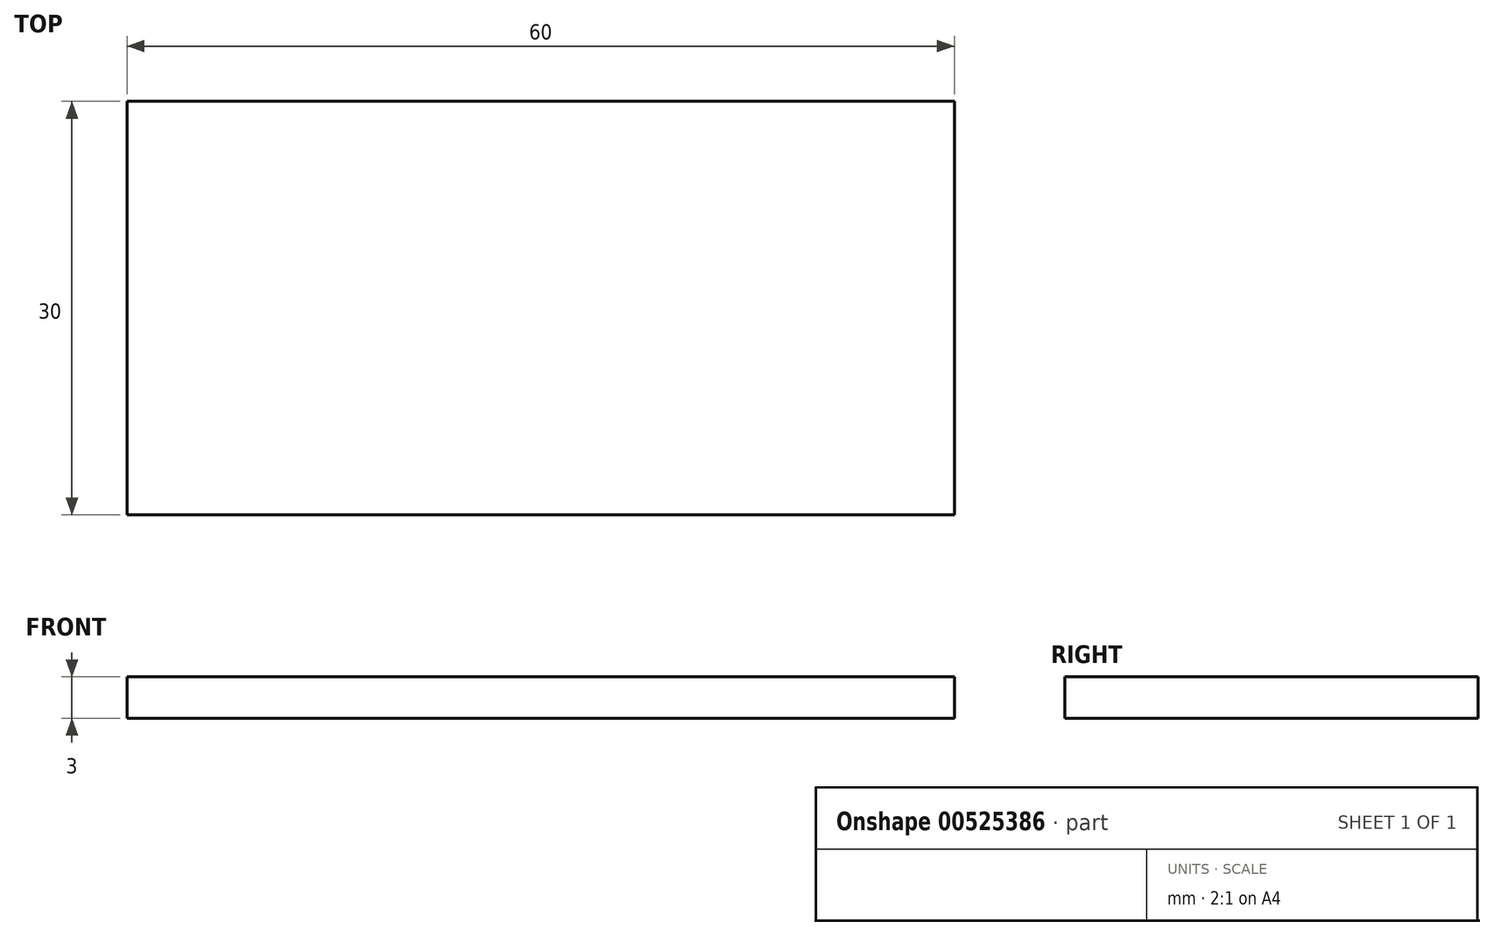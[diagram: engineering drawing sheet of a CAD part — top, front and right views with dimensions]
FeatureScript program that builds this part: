
annotation { "Feature Type Name" : "Feature", "Feature Type Description" : "" }
export const myFeature = defineFeature(function(context is Context, id is Id, definition is map)
    precondition{}
    {
        {
            var Q0;
            Q0=qCreatedBy(makeId("Top.planeOp"),FACE);
            var sketch = newSketch(context, id + "F0", { "sketchPlane" : qUnion([Q0])});
            skLineSegment(sketch, "E0.bottom", {"start": v(-30, -15) * mm, "end": v(30, -15) * mm});
            skLineSegment(sketch, "E0.top", {"start": v(-30, 15) * mm, "end": v(30, 15) * mm});
            skLineSegment(sketch, "E0.left", {"start": v(-30, -15) * mm, "end": v(-30, 15) * mm});
            skLineSegment(sketch, "E0.right", {"start": v(30, -15) * mm, "end": v(30, 15) * mm});
            skLineSegment(sketch, "E1", {"start": v(-30, 15) * mm, "end": v(0, 0) * mm, "construction": true});
            skLineSegment(sketch, "E2", {"start": v(0, 0) * mm, "end": v(30, -15) * mm, "construction": true});
            skLineSegment(sketch, "E3", {"start": v(-30, -15) * mm, "end": v(0, 0) * mm, "construction": true});
            skSolve(sketch);
        }
        {
            var Q0;
            Q0 = qSketchRegion(id + "F0", true);
            extrude(context, id + "F1", {"entities" : qUnion([Q0]), "depth" : 3 * mm, "offsetDistance" : 25.4 * mm});
        }
    });
